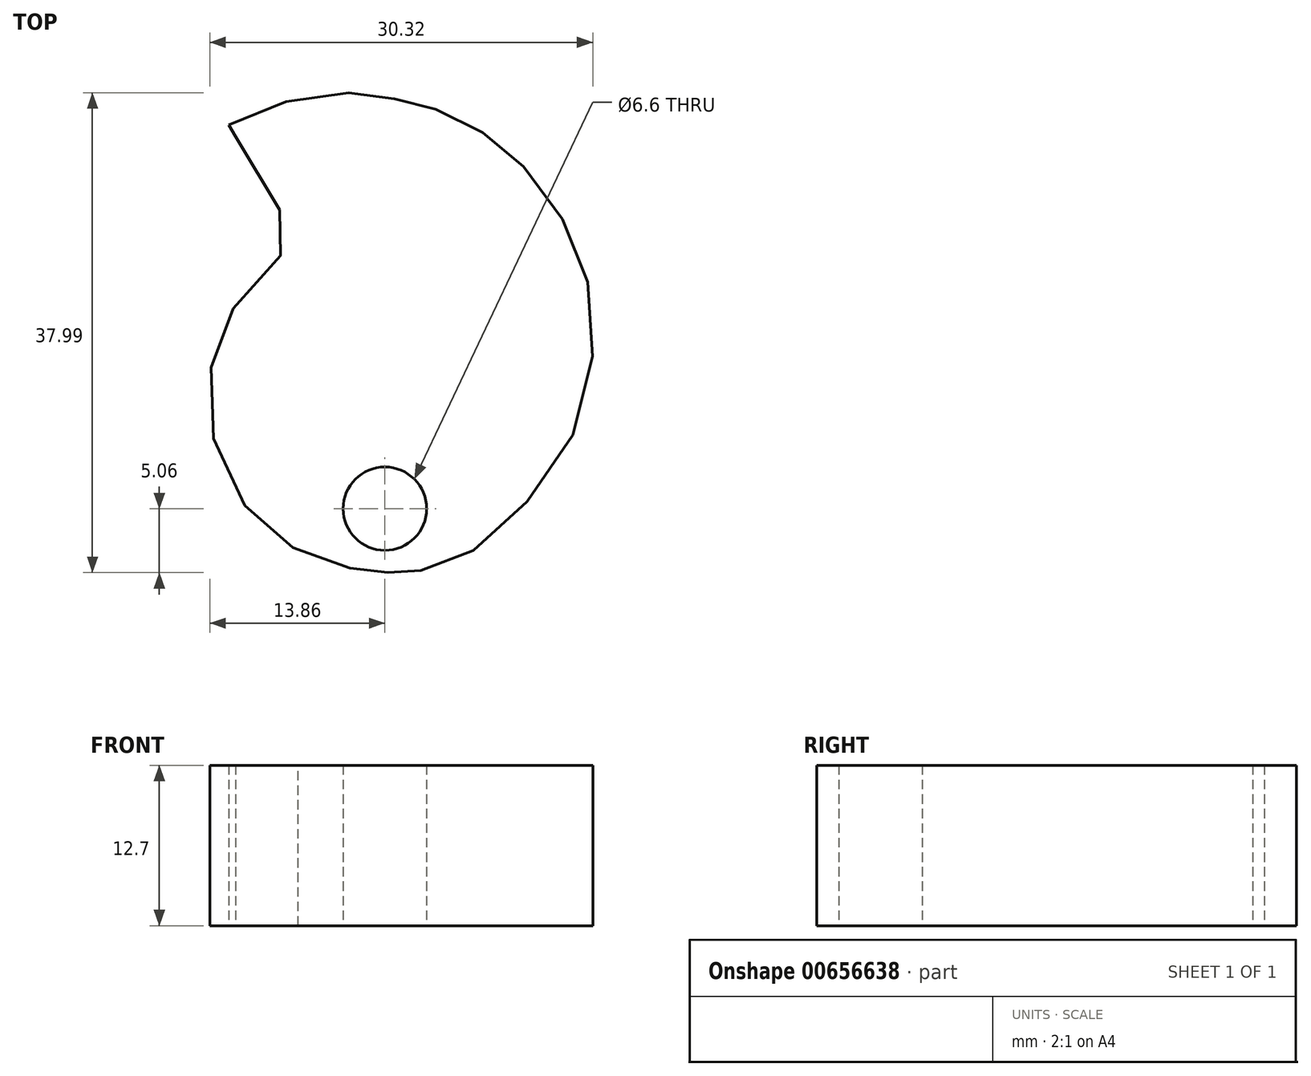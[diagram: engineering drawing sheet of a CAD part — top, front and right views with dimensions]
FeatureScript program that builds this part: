
annotation { "Feature Type Name" : "Feature", "Feature Type Description" : "" }
export const myFeature = defineFeature(function(context is Context, id is Id, definition is map)
    precondition{}
    {
        {
            var Q0;
            Q0=qCreatedBy(makeId("Top.planeOp"),FACE);
            var sketch = newSketch(context, id + "F0", { "sketchPlane" : qUnion([Q0])});
            skFitSpline(sketch, "E0", {"points": [v(-12.36, 30.4) * mm, v(-9.47, 31.68) * mm, v(-7.13, 32.4) * mm, v(-3.69, 32.92) * mm, v(-2.12, 32.87) * mm, v(-0.34, 32.66) * mm, v(1, 32.4) * mm, v(2.3, 32.1) * mm, v(3.57, 31.76) * mm, v(5.05, 31.25) * mm, v(7.03, 30.23) * mm, v(8.77, 29.06) * mm, v(10.34, 27.68) * mm, v(12.01, 26) * mm, v(13.95, 23.08) * mm, v(15.4, 20.26) * mm, v(16.3, 16.43) * mm, v(16.44, 12.36) * mm, v(15.78, 8.28) * mm, v(13.13, 2.68) * mm, v(10.75, 0) * mm, v(8.05, -2.7) * mm, v(4.14, -4.48) * mm, v(3.16, -4.79) * mm, v(2.18, -5.03) * mm, v(0.77, -5.03) * mm, v(0.56, -5.03) * mm, v(0.35, -5.04) * mm, v(-0.25, -5.02) * mm, v(-1.32, -4.95) * mm, v(-2.57, -4.76) * mm, v(-4.74, -4.16) * mm, v(-7.56, -2.94) * mm, v(-9.76, -1.35) * mm, v(-12.08, 1.84) * mm, v(-13.55, 5.5) * mm, v(-13.85, 9.73) * mm, v(-13.54, 12.3) * mm, v(-12.35, 15.21) * mm, v(-10.56, 17.87) * mm, v(-7.68, 20.38) * mm, v(-6.88, 20.87) * mm, v(-9.55, 25.45) * mm, v(-11.82, 29.47) * mm], "startDerivative": vector(113.8, 53.14) * mm, "endDerivative": vector(-56.9, 112.87) * mm});
            skLineSegment(sketch, "E1", {"start": v(-12.36, 30.4) * mm, "end": v(-11.82, 29.47) * mm});
            skCircle(sketch, "E2", {"center": v(0, 0) * mm, "radius": 3.3 * mm});
            skSolve(sketch);
        }
        {
            var Q0;
            Q0=makeQuery(id+"F0.imprint","IMPRINT",FACE,{"disambiguationData":[TD([[makeQuery(id+"F0.imprint","IMPRINT",EDGE,{"derivedFrom":sQuery(id+"F0.wireOp",EDGE,"E0")}),-1.0]])]});
            extrude(context, id + "F1", {"entities" : qUnion([Q0]), "depth" : 12.7 * mm, "offsetDistance" : 25.4 * mm});
        }
    });
